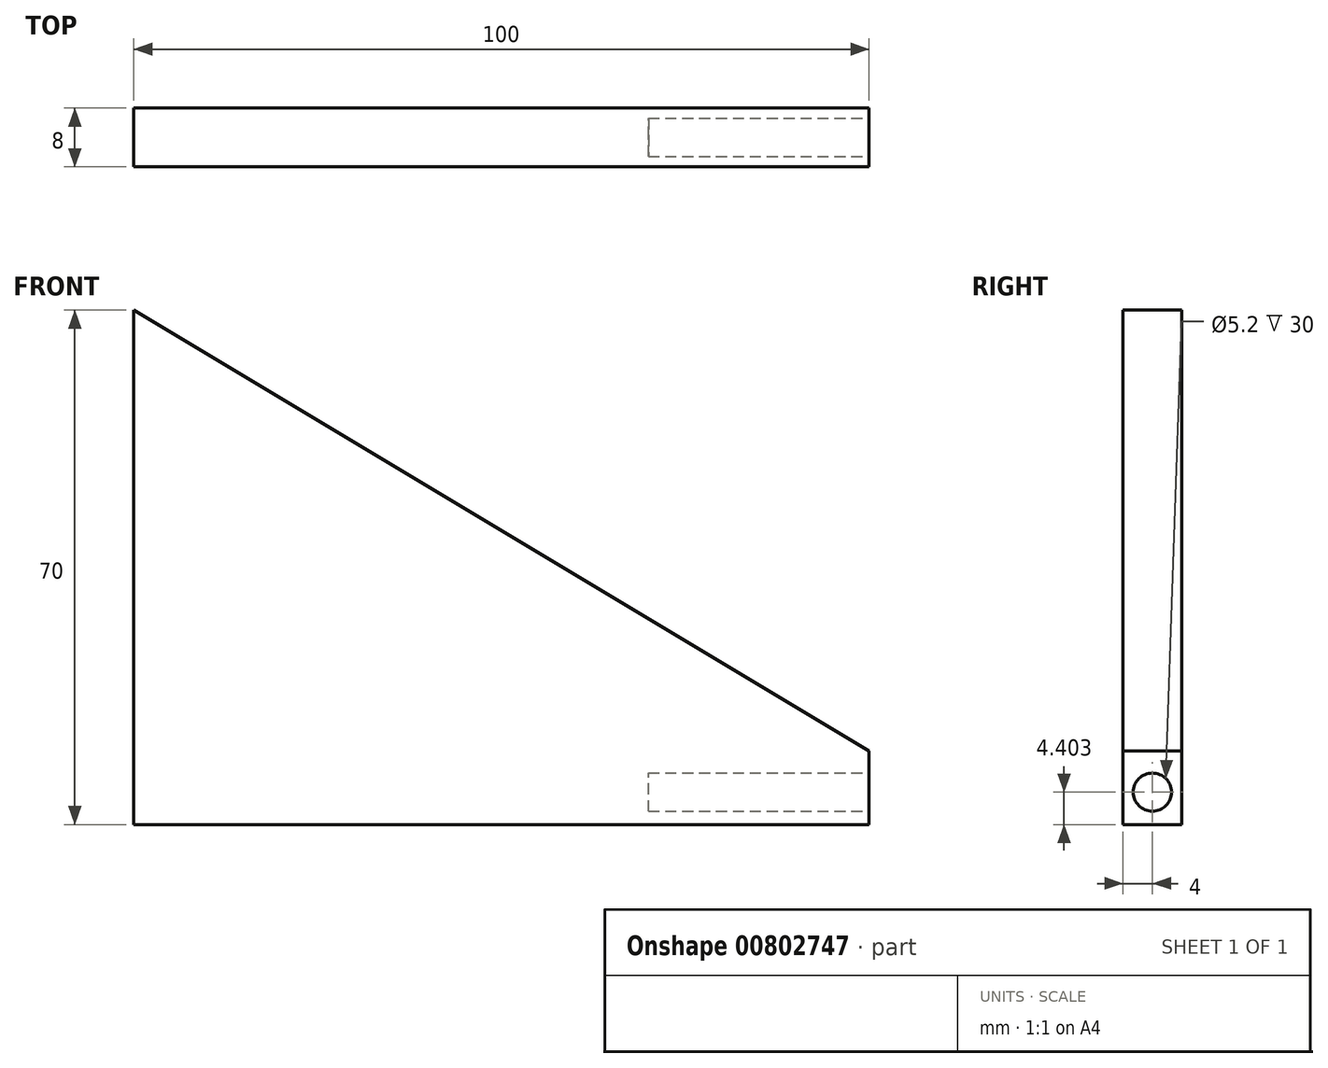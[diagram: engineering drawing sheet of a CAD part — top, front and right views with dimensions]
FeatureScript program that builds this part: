
annotation { "Feature Type Name" : "Feature", "Feature Type Description" : "" }
export const myFeature = defineFeature(function(context is Context, id is Id, definition is map)
    precondition{}
    {
        {
            var Q0;
            Q0=qCreatedBy(makeId("Front.planeOp"),FACE);
            var sketch = newSketch(context, id + "F0", { "sketchPlane" : qUnion([Q0])});
            skLineSegment(sketch, "E0", {"start": v(0, 0) * mm, "end": v(-100, 0) * mm});
            skLineSegment(sketch, "E1", {"start": v(-100, 0) * mm, "end": v(-100, 70) * mm});
            skLineSegment(sketch, "E2", {"start": v(-100, 70) * mm, "end": v(0, 10) * mm});
            skLineSegment(sketch, "E3", {"start": v(0, 10) * mm, "end": v(0, 0) * mm});
            skSolve(sketch);
        }
        {
            var Q0;
            Q0=makeQuery(id+"F0.imprint","IMPRINT",FACE,{"disambiguationData":[TD([[makeQuery(id+"F0.imprint","IMPRINT",EDGE,{"derivedFrom":sQuery(id+"F0.wireOp",EDGE,"E0")}),-1.0]])]});
            extrude(context, id + "F1", {"entities" : qUnion([Q0]), "depth" : 8 * mm, "offsetDistance" : 25 * mm});
        }
        {
            var Q0;
            Q0=makeQuery(id+"F1.opExtrude","SWEPT_FACE",FACE,{"disambiguationData":[OSD([sQuery(id+"F0.wireOp",EDGE,"E3")])]});
            var sketch = newSketch(context, id + "F2", { "sketchPlane" : qUnion([Q0])});
            skCircle(sketch, "E4", {"center": v(-4, 4.4) * mm, "radius": 2.6 * mm});
            skPoint(sketch, "E4.centerSnap0", {"position": v(-4, 0) * mm});
            skSolve(sketch);
        }
        {
            var Q0;
            Q0 = qSketchRegion(id + "F2", true);
            extrude(context, id + "F3", {"entities" : qUnion([Q0]), "operationType" : NewBodyOperationType.REMOVE, "oppositeDirection" : true, "depth" : 30 * mm, "offsetDistance" : 25 * mm});
        }
    });
